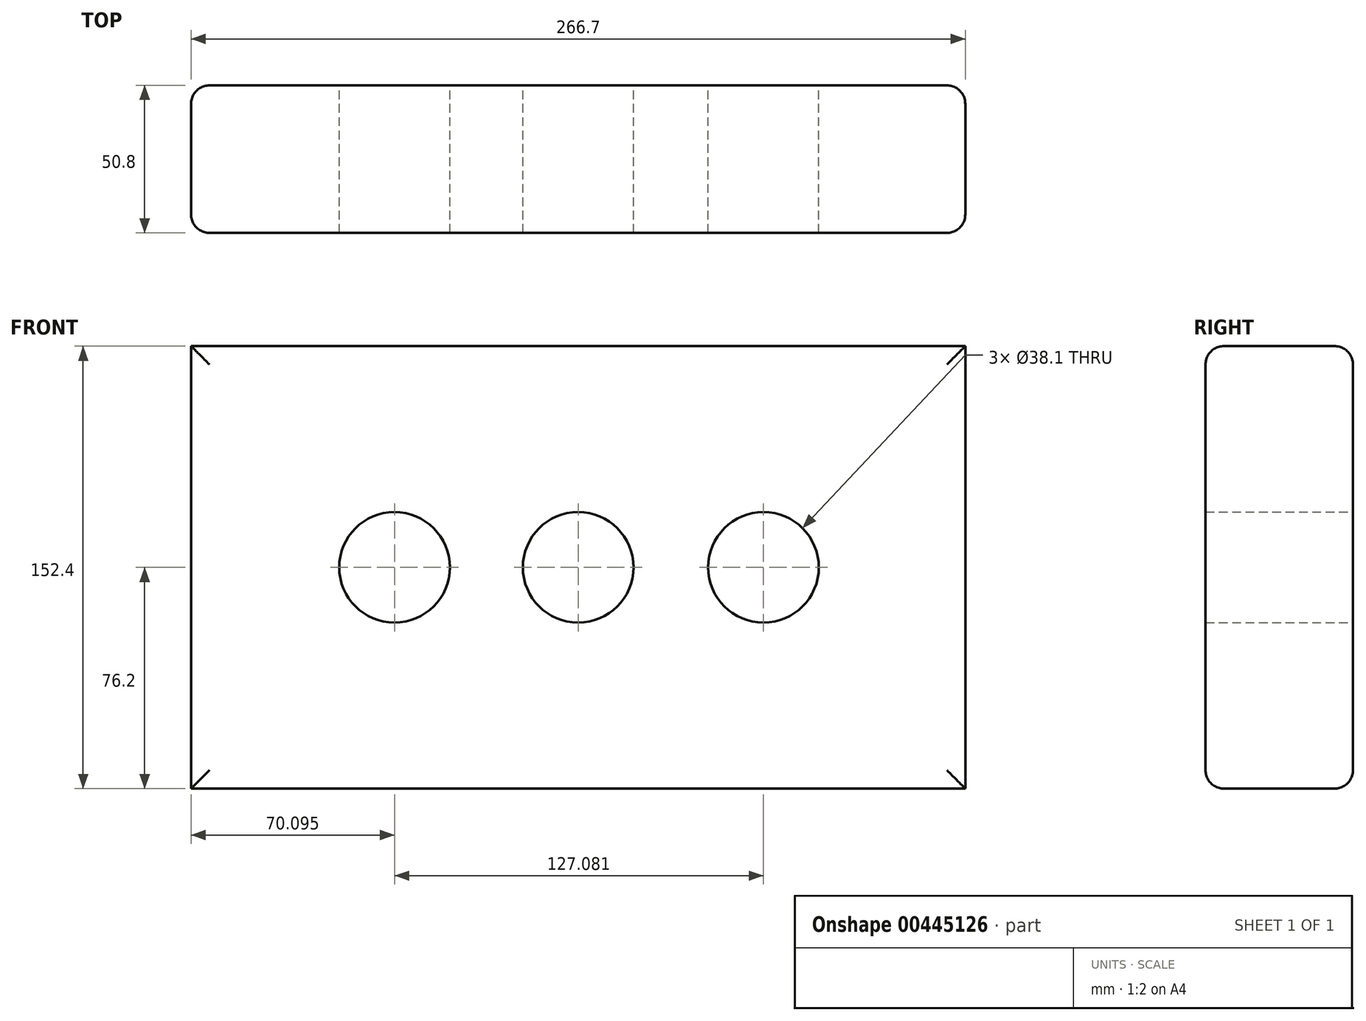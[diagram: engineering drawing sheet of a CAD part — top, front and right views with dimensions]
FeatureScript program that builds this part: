
annotation { "Feature Type Name" : "Feature", "Feature Type Description" : "" }
export const myFeature = defineFeature(function(context is Context, id is Id, definition is map)
    precondition{}
    {
        {
            var Q0;
            Q0=qCreatedBy(makeId("Front.planeOp"),FACE);
            var sketch = newSketch(context, id + "F0", { "sketchPlane" : qUnion([Q0])});
            skLineSegment(sketch, "E0.bottom", {"start": v(-133.35, 76.2) * mm, "end": v(133.35, 76.2) * mm});
            skLineSegment(sketch, "E0.top", {"start": v(-133.35, -76.2) * mm, "end": v(133.35, -76.2) * mm});
            skLineSegment(sketch, "E0.left", {"start": v(-133.35, 76.2) * mm, "end": v(-133.35, -76.2) * mm});
            skLineSegment(sketch, "E0.right", {"start": v(133.35, 76.2) * mm, "end": v(133.35, -76.2) * mm});
            skPoint(sketch, "E0.middle", {"position": v(0, 0) * mm});
            skCircle(sketch, "E1", {"center": v(0, 0) * mm, "radius": 19.05 * mm});
            skLineSegment(sketch, "E2", {"start": v(19.05, 0) * mm, "end": v(44.45, 0) * mm});
            skPoint(sketch, "E2.startSnap0", {"position": v(133.35, 0) * mm});
            skPoint(sketch, "E2.endSnap0", {"position": v(133.35, 0) * mm});
            skCircle(sketch, "E3", {"center": v(63.83, 0) * mm, "radius": 19.05 * mm});
            skLineSegment(sketch, "E4", {"start": v(-19.05, 0) * mm, "end": v(-44.45, 0) * mm});
            skCircle(sketch, "E5", {"center": v(-63.25, 0) * mm, "radius": 19.05 * mm});
            skSolve(sketch);
        }
        {
            var Q0;
            Q0 = qSketchRegion(id + "F0", true);
            extrude(context, id + "F1", {"entities" : qUnion([Q0]), "depth" : 50.8 * mm});
        }
        {
            var Q0;
            Q0=makeQuery(id+"F1.opExtrude","CAP_EDGE",EDGE,{"disambiguationData":[OSD([sQuery(id+"F0.wireOp",EDGE,"E0.top")])],"isStart":false});
            var Q1;
            Q1=makeQuery(id+"F1.opExtrude","CAP_EDGE",EDGE,{"disambiguationData":[OSD([sQuery(id+"F0.wireOp",EDGE,"E0.right")])],"isStart":false});
            var Q2;
            Q2=makeQuery(id+"F1.opExtrude","CAP_EDGE",EDGE,{"disambiguationData":[OSD([sQuery(id+"F0.wireOp",EDGE,"E0.bottom")])],"isStart":false});
            var Q3;
            Q3=makeQuery(id+"F1.opExtrude","CAP_EDGE",EDGE,{"disambiguationData":[OSD([sQuery(id+"F0.wireOp",EDGE,"E0.left")])],"isStart":false});
            var Q4;
            Q4=makeQuery(id+"F1.opExtrude","CAP_EDGE",EDGE,{"disambiguationData":[OSD([sQuery(id+"F0.wireOp",EDGE,"E0.bottom")])],"isStart":true});
            var Q5;
            Q5=makeQuery(id+"F1.opExtrude","CAP_EDGE",EDGE,{"disambiguationData":[OSD([sQuery(id+"F0.wireOp",EDGE,"E0.right")])],"isStart":true});
            var Q6;
            Q6=makeQuery(id+"F1.opExtrude","CAP_EDGE",EDGE,{"disambiguationData":[OSD([sQuery(id+"F0.wireOp",EDGE,"E0.top")])],"isStart":true});
            var Q7;
            Q7=makeQuery(id+"F1.opExtrude","CAP_EDGE",EDGE,{"disambiguationData":[OSD([sQuery(id+"F0.wireOp",EDGE,"E0.left")])],"isStart":true});
            fillet(context, id + "F2", {"entities" : qUnion([Q0, Q1, Q2, Q3, Q4, Q5, Q6, Q7]), "radius" : 6.35 * mm, "tangentPropagation" : true, "allowEdgeOverflow" : false});
        }
    });
